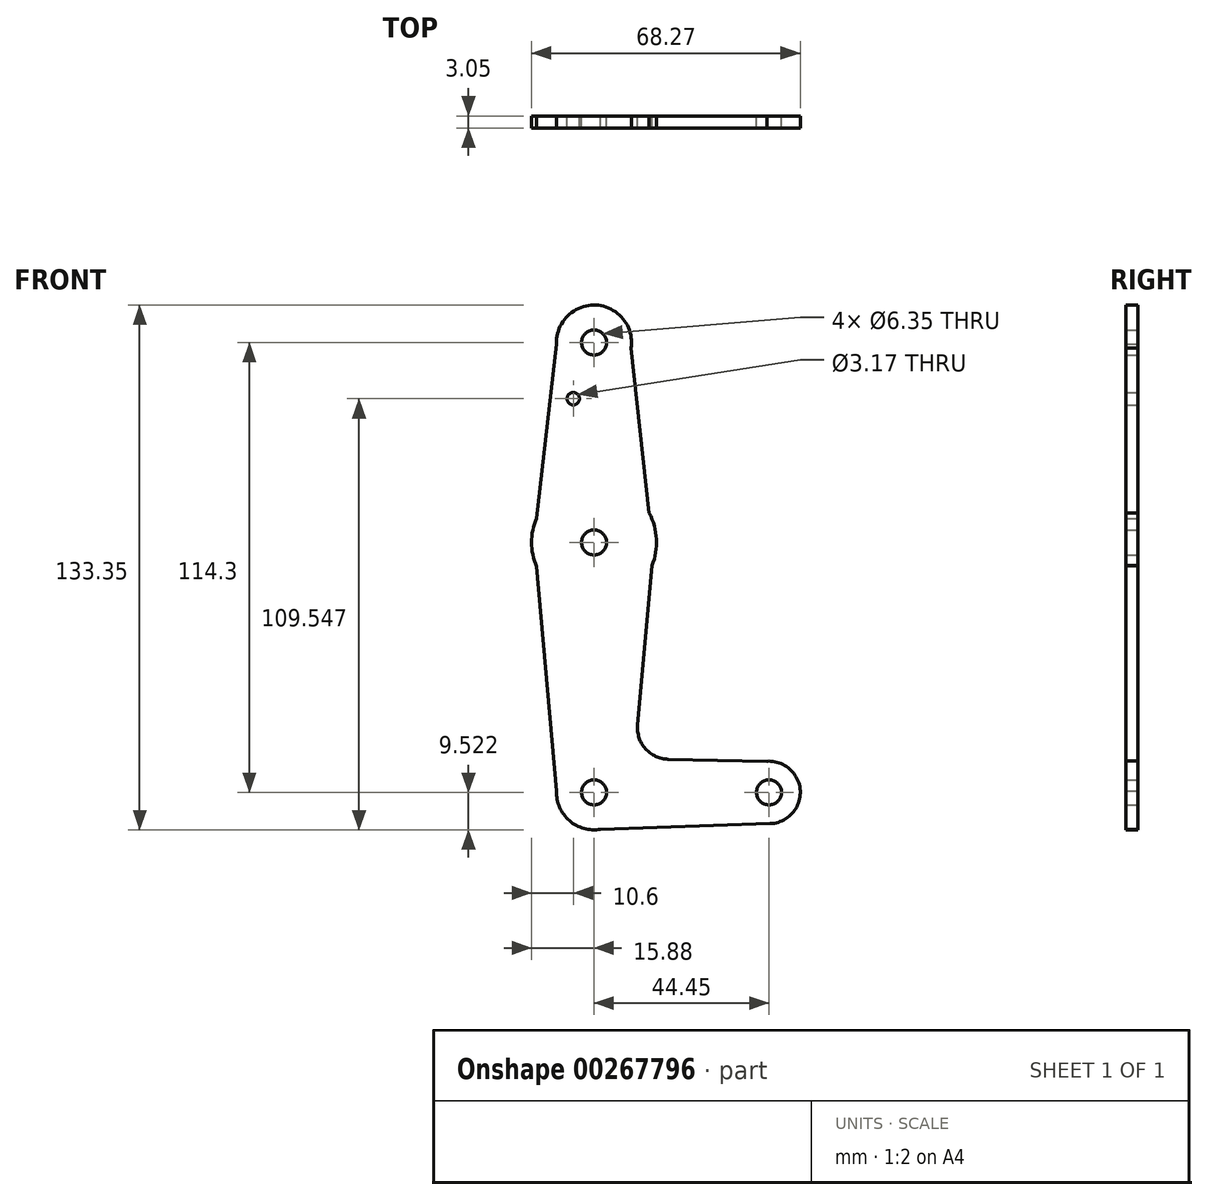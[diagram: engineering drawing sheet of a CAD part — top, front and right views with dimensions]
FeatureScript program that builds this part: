
annotation { "Feature Type Name" : "Feature", "Feature Type Description" : "" }
export const myFeature = defineFeature(function(context is Context, id is Id, definition is map)
    precondition{}
    {
        {
            var Q0;
            Q0=qCreatedBy(makeId("Front.planeOp"),FACE);
            var sketch = newSketch(context, id + "F0", { "sketchPlane" : qUnion([Q0])});
            skLineSegment(sketch, "E0", {"start": v(0, 68.98) * mm, "end": v(0, -45.32) * mm});
            skLineSegment(sketch, "E1", {"start": v(0, -45.32) * mm, "end": v(44.45, -45.32) * mm});
            skCircle(sketch, "E2", {"center": v(0, 68.98) * mm, "radius": 9.53 * mm});
            skCircle(sketch, "E3", {"center": v(0, 18.18) * mm, "radius": 15.88 * mm});
            skCircle(sketch, "E4", {"center": v(0, -45.32) * mm, "radius": 9.53 * mm});
            skCircle(sketch, "E5", {"center": v(44.45, -45.32) * mm, "radius": 7.94 * mm});
            skLineSegment(sketch, "E6", {"start": v(-9.52, 68.63) * mm, "end": v(-14.64, 24.32) * mm});
            skLineSegment(sketch, "E7", {"start": v(9.42, 67.6) * mm, "end": v(14.02, 25.63) * mm});
            skLineSegment(sketch, "E8", {"start": v(-9.52, -44.99) * mm, "end": v(-14.64, 12.04) * mm});
            skLineSegment(sketch, "E9", {"start": v(11.07, -28.22) * mm, "end": v(14.73, 12.27) * mm});
            skLineSegment(sketch, "E10", {"start": v(43.88, -37.4) * mm, "end": v(18.83, -36.89) * mm});
            skLineSegment(sketch, "E11", {"start": v(44.72, -53.25) * mm, "end": v(1.63, -54.7) * mm});
            skArc(sketch, "E12.filletArc", {"start": v(11.07, -28.22) * mm, "mid": v(13.07, -34.24) * mm, "end": v(18.83, -36.89) * mm});
            skCircle(sketch, "E13", {"center": v(0, 68.98) * mm, "radius": 3.18 * mm});
            skCircle(sketch, "E14", {"center": v(0, 18.18) * mm, "radius": 3.18 * mm});
            skCircle(sketch, "E15", {"center": v(0, -45.32) * mm, "radius": 3.18 * mm});
            skCircle(sketch, "E16", {"center": v(44.45, -45.32) * mm, "radius": 3.18 * mm});
            skCircle(sketch, "E17", {"center": v(-5.28, 54.7) * mm, "radius": 1.59 * mm});
            skSolve(sketch);
        }
        {
            var Q0;
            Q0 = qSketchRegion(id + "F0", true);
            var Q1;
            {var subQ0=sQuery(id+"F0.wireOp",EDGE,"E4");var subQ1=sQuery(id+"F0.wireOp",EDGE,"E0");var subQ2=makeQuery(id+"F0.imprint","INTERSECT",VERTEX,{"derivedFrom":[subQ1,subQ0]});Q1=makeQuery(id+"F0.imprint","IMPRINT",FACE,{"disambiguationData":[TD([[makeQuery(id+"F0.imprint","IMPRINT",EDGE,{"disambiguationData":[TD([[subQ2,-1.0]])],"derivedFrom":subQ1}),1.0]])]});}
            extrude(context, id + "F1", {"entities" : qUnion([Q0, Q1]), "depth" : 3.05 * mm});
        }
    });
